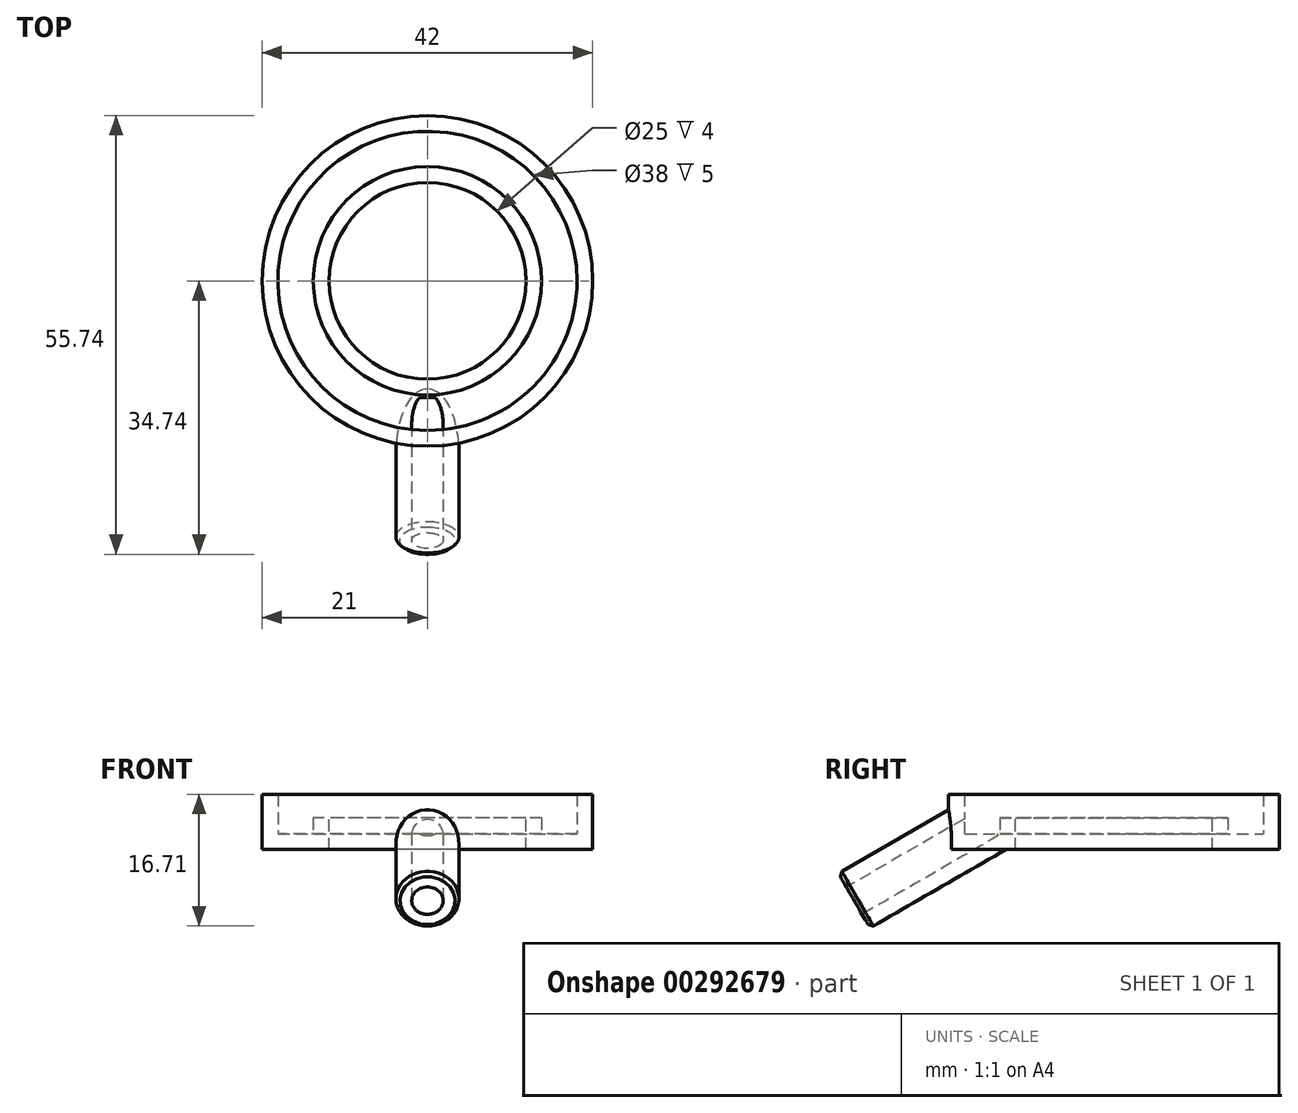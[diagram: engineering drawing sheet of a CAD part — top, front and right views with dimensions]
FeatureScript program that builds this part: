
annotation { "Feature Type Name" : "Feature", "Feature Type Description" : "" }
export const myFeature = defineFeature(function(context is Context, id is Id, definition is map)
    precondition{}
    {
        {
            var Q0;
            Q0=qCreatedBy(makeId("Top.planeOp"),FACE);
            var sketch = newSketch(context, id + "F0", { "sketchPlane" : qUnion([Q0])});
            skCircle(sketch, "E0", {"center": v(0, 0) * mm, "radius": 12.5 * mm});
            skCircle(sketch, "E1", {"center": v(0, 0) * mm, "radius": 14.5 * mm});
            skCircle(sketch, "E2", {"center": v(0, 0) * mm, "radius": 19 * mm});
            skCircle(sketch, "E3", {"center": v(0, 0) * mm, "radius": 21 * mm});
            skSolve(sketch);
        }
        {
            var Q0;
            Q0=makeQuery(id+"F0.imprint","IMPRINT",FACE,{"disambiguationData":[TD([[makeQuery(id+"F0.imprint","IMPRINT",EDGE,{"derivedFrom":sQuery(id+"F0.wireOp",EDGE,"E2")}),-1.0]])]});
            var Q1;
            Q1=makeQuery(id+"F0.imprint","IMPRINT",FACE,{"disambiguationData":[TD([[makeQuery(id+"F0.imprint","IMPRINT",EDGE,{"derivedFrom":sQuery(id+"F0.wireOp",EDGE,"E1")}),-1.0]])]});
            var Q2;
            Q2=makeQuery(id+"F0.imprint","IMPRINT",FACE,{"disambiguationData":[TD([[makeQuery(id+"F0.imprint","IMPRINT",EDGE,{"derivedFrom":sQuery(id+"F0.wireOp",EDGE,"E0")}),-1.0]])]});
            extrude(context, id + "F1", {"entities" : qUnion([Q0, Q1, Q2]), "oppositeDirection" : true, "depth" : 2 * mm, "offsetDistance" : 25 * mm});
        }
        {
            var Q0;
            Q0=makeQuery(id+"F0.imprint","IMPRINT",FACE,{"disambiguationData":[TD([[makeQuery(id+"F0.imprint","IMPRINT",EDGE,{"derivedFrom":sQuery(id+"F0.wireOp",EDGE,"E0")}),-1.0]])]});
            extrude(context, id + "F2", {"entities" : qUnion([Q0]), "operationType" : NewBodyOperationType.ADD, "depth" : 2 * mm, "offsetDistance" : 25 * mm});
        }
        {
            var Q0;
            Q0=makeQuery(id+"F0.imprint","IMPRINT",FACE,{"disambiguationData":[TD([[makeQuery(id+"F0.imprint","IMPRINT",EDGE,{"derivedFrom":sQuery(id+"F0.wireOp",EDGE,"E2")}),-1.0]])]});
            extrude(context, id + "F3", {"entities" : qUnion([Q0]), "operationType" : NewBodyOperationType.ADD, "depth" : 5 * mm, "offsetDistance" : 25 * mm});
        }
        {
            var Q0;
            Q0=qCreatedBy(makeId("Right.planeOp"),FACE);
            var sketch = newSketch(context, id + "F4", { "sketchPlane" : qUnion([Q0])});
            skLineSegment(sketch, "E4", {"start": v(-20, -1) * mm, "end": v(-33, -8.5) * mm});
            skSolve(sketch);
        }
        {
            var Q0;
            Q0=sQuery(id+"F4.wireOp",VERTEX,"E4.start");
            var Q1;
            Q1=sQuery(id+"F4.wireOp",EDGE,"E4");
            cPlane(context, id + "F5", {"entities" : qUnion([Q0, Q1]), "cplaneType" : CPlaneType.LINE_POINT, "offset" : 25 * mm, "width" : 150 * mm, "height" : 150 * mm});
        }
        {
            var Q0;
            Q0=qCreatedBy(id+"F5.planeOp",FACE);
            var sketch = newSketch(context, id + "F6", { "sketchPlane" : qUnion([Q0])});
            skCircle(sketch, "E5", {"center": v(0, 9.13) * mm, "radius": 4 * mm});
            skCircle(sketch, "E6", {"center": v(0, 9.13) * mm, "radius": 2 * mm});
            skSolve(sketch);
        }
        {
            var Q0;
            Q0=makeQuery(id+"F6.imprint","IMPRINT",FACE,{"disambiguationData":[TD([[makeQuery(id+"F6.imprint","IMPRINT",EDGE,{"derivedFrom":sQuery(id+"F6.wireOp",EDGE,"E5")}),1.0]])]});
            var Q1;
            Q1=makeQuery(id+"F1.opExtrude","SWEPT_BODY",BODY,{"disambiguationData":[OSD([sQuery(id+"F0.wireOp",EDGE,"E0"),sQuery(id+"F0.wireOp",EDGE,"E3")])]});
            extrude(context, id + "F7", {"entities" : qUnion([Q0]), "operationType" : NewBodyOperationType.ADD, "endBound" : BoundingType.UP_TO_BODY, "oppositeDirection" : true, "depth" : 25 * mm, "endBoundEntityBody" : qUnion([Q1]), "offsetDistance" : 25 * mm});
        }
        {
            var Q0;
            Q0=makeQuery(id+"F6.imprint","IMPRINT",FACE,{"disambiguationData":[TD([[makeQuery(id+"F6.imprint","IMPRINT",EDGE,{"derivedFrom":sQuery(id+"F6.wireOp",EDGE,"E5")}),1.0]])]});
            extrude(context, id + "F8", {"entities" : qUnion([Q0]), "operationType" : NewBodyOperationType.ADD, "depth" : 15 * mm, "offsetDistance" : 25 * mm});
        }
        {
            var Q0;
            Q0=makeQuery(id+"F8.opExtrude","CAP_EDGE",EDGE,{"disambiguationData":[OSD([sQuery(id+"F6.wireOp",EDGE,"E5")])],"isStart":false});
            chamfer(context, id + "F9", {"entities" : qUnion([Q0]), "width" : 0.5 * mm, "tangentPropagation" : true});
        }
        {
            var Q0;
            Q0=makeQuery(id+"F6.imprint","IMPRINT",FACE,{"disambiguationData":[TD([[makeQuery(id+"F6.imprint","IMPRINT",EDGE,{"derivedFrom":sQuery(id+"F6.wireOp",EDGE,"E6")}),1.0]])]});
            extrude(context, id + "F10", {"entities" : qUnion([Q0]), "operationType" : NewBodyOperationType.REMOVE, "oppositeDirection" : true, "depth" : 5 * mm, "offsetDistance" : 25 * mm, "hasSecondDirection" : true, "secondDirectionOppositeDirection" : false, "secondDirectionDepth" : 25 * mm});
        }
    });
